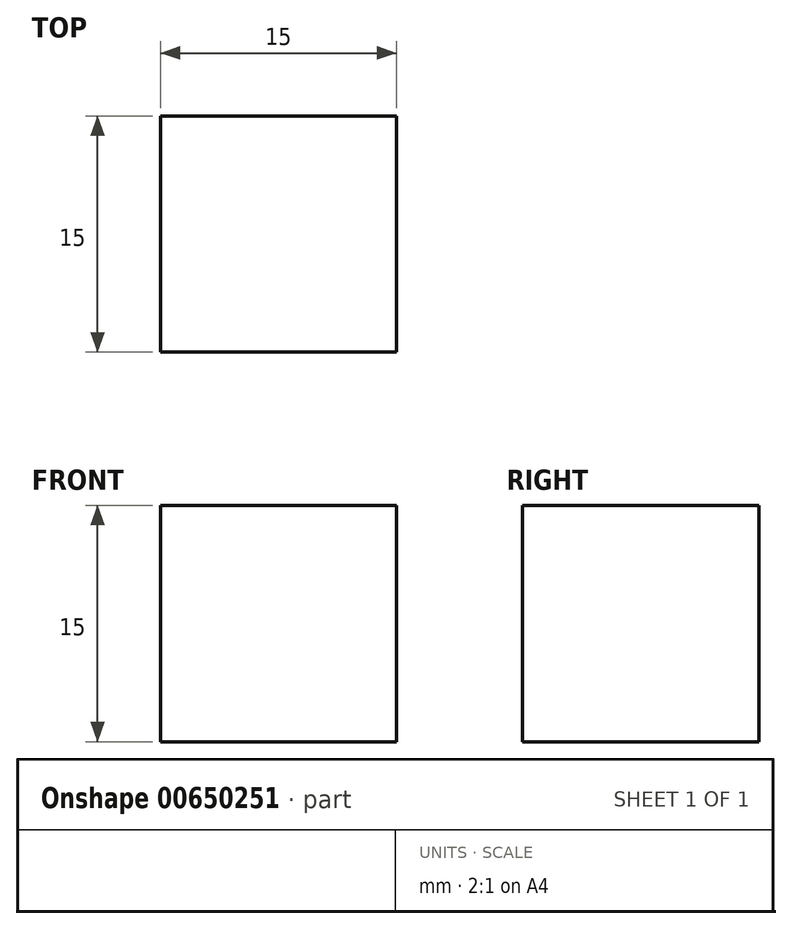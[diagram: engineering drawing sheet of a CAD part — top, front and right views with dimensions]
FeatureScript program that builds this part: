
annotation { "Feature Type Name" : "Feature", "Feature Type Description" : "" }
export const myFeature = defineFeature(function(context is Context, id is Id, definition is map)
    precondition{}
    {
        {
            var Q0;
            Q0=qCreatedBy(makeId("Top.planeOp"),FACE);
            var sketch = newSketch(context, id + "F0", { "sketchPlane" : qUnion([Q0])});
            skLineSegment(sketch, "E0.bottom", {"start": v(7.5, -7.5) * mm, "end": v(-7.5, -7.5) * mm});
            skLineSegment(sketch, "E0.top", {"start": v(7.5, 7.5) * mm, "end": v(-7.5, 7.5) * mm});
            skLineSegment(sketch, "E0.left", {"start": v(7.5, -7.5) * mm, "end": v(7.5, 7.5) * mm});
            skLineSegment(sketch, "E0.right", {"start": v(-7.5, -7.5) * mm, "end": v(-7.5, 7.5) * mm});
            skPoint(sketch, "E0.middle", {"position": v(0, 0) * mm});
            skSolve(sketch);
        }
        {
            var Q0;
            Q0 = qSketchRegion(id + "F0", true);
            extrude(context, id + "F1", {"entities" : qUnion([Q0]), "depth" : 15 * mm, "offsetDistance" : 25 * mm});
        }
    });
